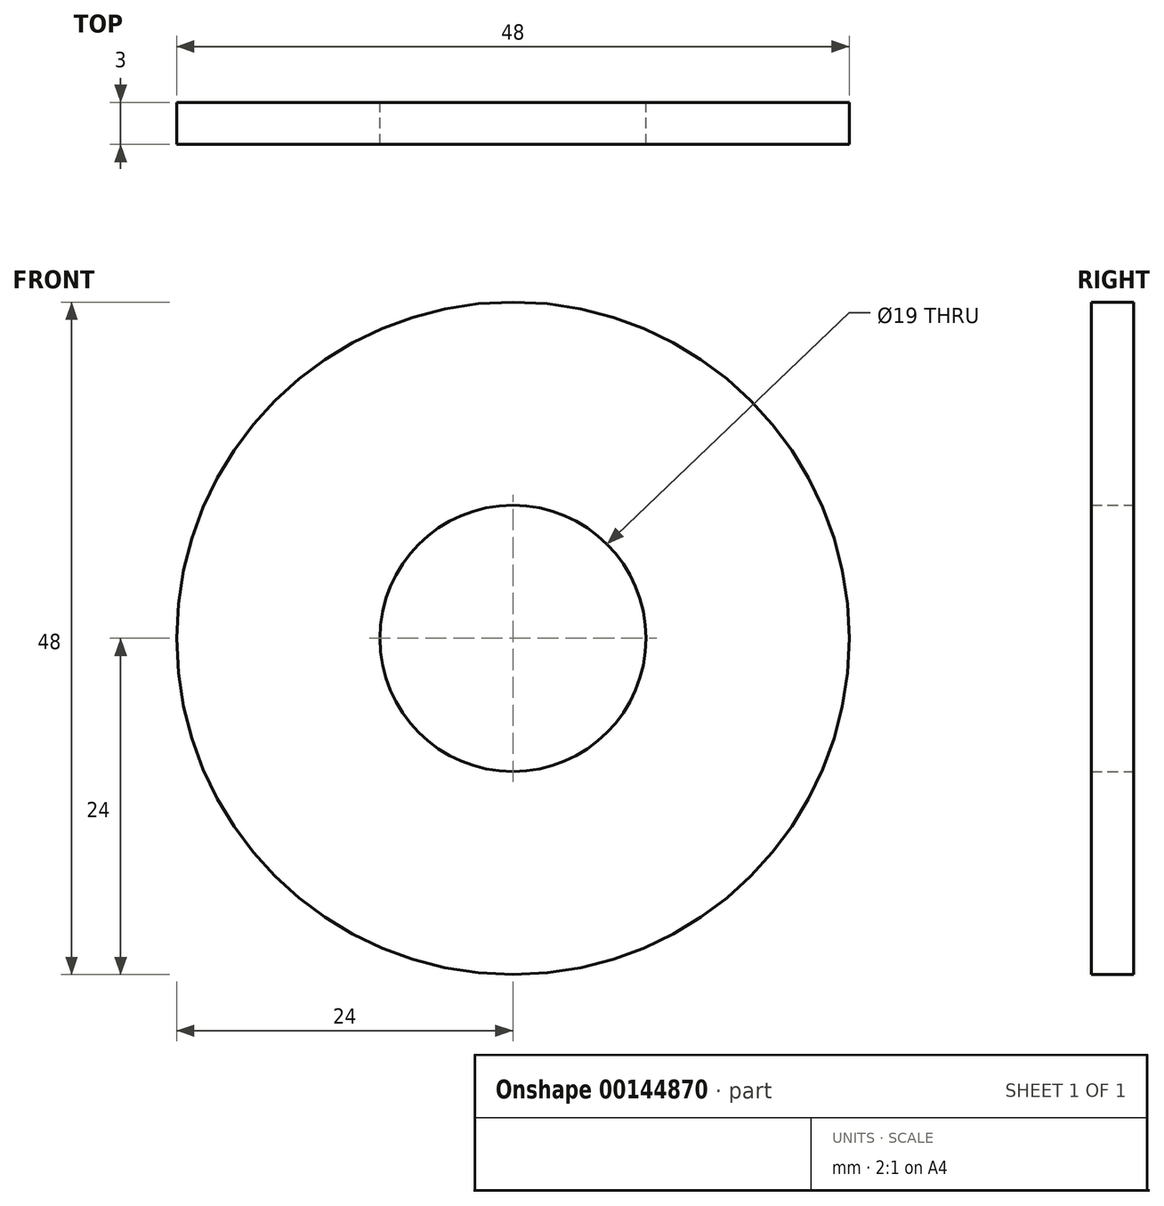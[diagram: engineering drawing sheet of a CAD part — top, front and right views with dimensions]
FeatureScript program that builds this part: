
annotation { "Feature Type Name" : "Feature", "Feature Type Description" : "" }
export const myFeature = defineFeature(function(context is Context, id is Id, definition is map)
    precondition{}
    {
        {
            var Q0;
            Q0=qCreatedBy(makeId("Front.planeOp"),FACE);
            var sketch = newSketch(context, id + "F0", { "sketchPlane" : qUnion([Q0])});
            skCircle(sketch, "E0", {"center": v(0, 0) * mm, "radius": 9.5 * mm});
            skCircle(sketch, "E1", {"center": v(0, 0) * mm, "radius": 24 * mm});
            skSolve(sketch);
        }
        {
            var Q0;
            Q0=qSketchRegion(id+"F0",true);
            extrude(context, id + "F1", {"entities" : qUnion([Q0]), "depth" : 3 * mm});
        }
    });
